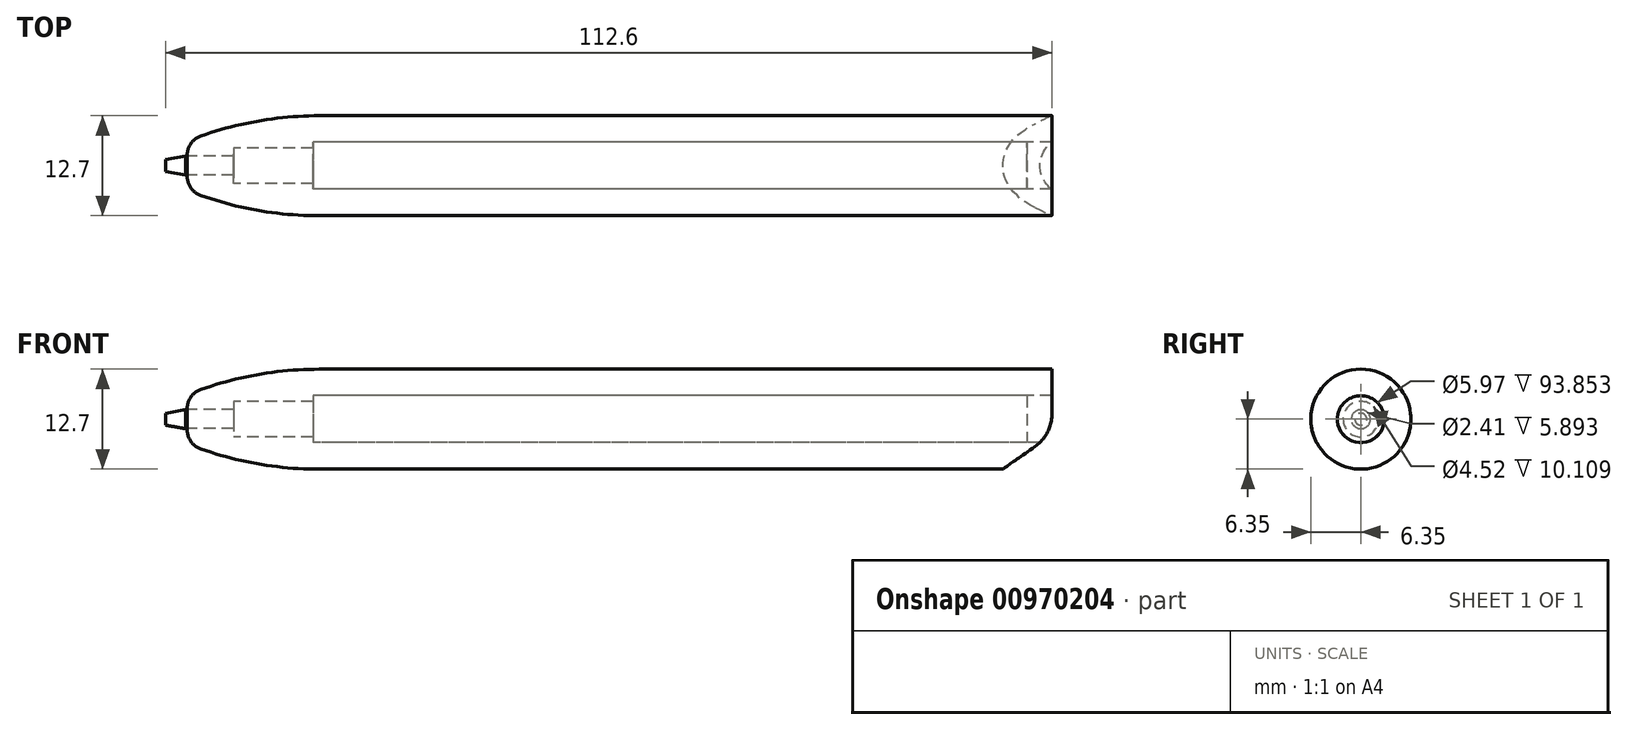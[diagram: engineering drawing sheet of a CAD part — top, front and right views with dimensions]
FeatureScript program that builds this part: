
annotation { "Feature Type Name" : "Feature", "Feature Type Description" : "" }
export const myFeature = defineFeature(function(context is Context, id is Id, definition is map)
    precondition{}
    {
        {
            var Q0;
            Q0=qCreatedBy(makeId("Front.planeOp"),FACE);
            var sketch = newSketch(context, id + "F0", { "sketchPlane" : qUnion([Q0])});
            skLineSegment(sketch, "E0", {"start": v(0, 0) * mm, "end": v(0, 2.98) * mm});
            skLineSegment(sketch, "E1", {"start": v(0, 2.98) * mm, "end": v(-90.68, 2.98) * mm});
            skLineSegment(sketch, "E2", {"start": v(-90.68, 2.98) * mm, "end": v(-90.68, 2.26) * mm});
            skLineSegment(sketch, "E3", {"start": v(-90.68, 2.26) * mm, "end": v(-100.79, 2.26) * mm});
            skLineSegment(sketch, "E4", {"start": v(-100.79, 1.55) * mm, "end": v(-100.79, 1.2) * mm});
            skLineSegment(sketch, "E5", {"start": v(-100.79, 1.2) * mm, "end": v(-109.42, 1.2) * mm});
            skLineSegment(sketch, "E6", {"start": v(-109.42, 1.2) * mm, "end": v(-109.42, 0) * mm});
            skLineSegment(sketch, "E7", {"start": v(-109.42, 0) * mm, "end": v(0, 0) * mm});
            skLineSegment(sketch, "E8", {"start": v(-100.79, 1.55) * mm, "end": v(-100.79, 2.26) * mm});
            skSolve(sketch);
        }
        {
            var Q0;
            Q0=makeQuery(id+"F0.imprint","IMPRINT",FACE,{"disambiguationData":[TD([[makeQuery(id+"F0.imprint","IMPRINT",EDGE,{"derivedFrom":sQuery(id+"F0.wireOp",EDGE,"E0")}),1.0]])]});
            var Q1;
            Q1=sQuery(id+"F0.wireOp",EDGE,"E7");
            revolve(context, id + "F1", {"surfaceOperationType" : NewSurfaceOperationType.NEW, "entities" : qUnion([Q0]), "axis" : qUnion([Q1]), "revolveType" : RevolveType.FULL});
        }
        {
            var Q0;
            Q0=qCreatedBy(makeId("Front.planeOp"),FACE);
            var sketch = newSketch(context, id + "F2", { "sketchPlane" : qUnion([Q0])});
            skLineSegment(sketch, "E9", {"start": v(-89.9, 6.35) * mm, "end": v(0, 6.35) * mm});
            skArc(sketch, "E10", {"start": v(-89.9, 6.35) * mm, "mid": v(-98.44, 5.54) * mm, "end": v(-106.68, 3.12) * mm});
            skLineSegment(sketch, "E11", {"start": v(-106.68, 3.12) * mm, "end": v(-106.68, 0) * mm});
            skLineSegment(sketch, "E12", {"start": v(-106.68, 0) * mm, "end": v(0, 0) * mm});
            skPoint(sketch, "E13.end.orphan", {"position": v(2.22, 6.35) * mm});
            skPoint(sketch, "E14.orphan", {"position": v(4.43, 6.35) * mm});
            skLineSegment(sketch, "E15", {"start": v(3.17, 0) * mm, "end": v(0, 0) * mm});
            skLineSegment(sketch, "E16", {"start": v(3.17, 0) * mm, "end": v(3.17, 6.35) * mm});
            skLineSegment(sketch, "E17", {"start": v(0, 6.35) * mm, "end": v(3.17, 6.35) * mm});
            skLineSegment(sketch, "E18.trimOffspring", {"start": v(4.36, 6.35) * mm, "end": v(4.43, 6.35) * mm});
            skSolve(sketch);
        }
        {
            var Q0;
            Q0=makeQuery(id+"F2.imprint","IMPRINT",FACE,{"disambiguationData":[TD([[makeQuery(id+"F2.imprint","IMPRINT",EDGE,{"derivedFrom":sQuery(id+"F2.wireOp",EDGE,"E9")}),-1.0]])]});
            var Q1;
            Q1=sQuery(id+"F2.wireOp",EDGE,"E9");
            var Q2;
            Q2=sQuery(id+"F2.wireOp",EDGE,"E10");
            var Q3;
            Q3=sQuery(id+"F2.wireOp",EDGE,"dEFs5qWQ-R8ky-eBhA-kIVd-nnHbt8vh1iMr");
            var Q4;
            Q4=sQuery(id+"F2.wireOp",EDGE,"E12");
            revolve(context, id + "F3", {"surfaceOperationType" : NewSurfaceOperationType.NEW, "entities" : qUnion([Q0]), "surfaceEntities" : qUnion([Q1, Q2, Q3]), "axis" : qUnion([Q4]), "revolveType" : RevolveType.FULL});
        }
        {
            var Q0;
            Q0=makeQuery(id+"F1.opRevolve","SWEPT_BODY",BODY,{"disambiguationData":[OSD([sQuery(id+"F0.wireOp",EDGE,"E0"),sQuery(id+"F0.wireOp",EDGE,"E1"),sQuery(id+"F0.wireOp",EDGE,"E2"),sQuery(id+"F0.wireOp",EDGE,"E3"),sQuery(id+"F0.wireOp",EDGE,"Mx4sm8FD-Cdkv-Anm1-aOvd-fS2C102Q7HrE"),sQuery(id+"F0.wireOp",EDGE,"LEFf2v4t-dNlz-Nh56-ndEK-DlUtqeBaB3i8"),sQuery(id+"F0.wireOp",EDGE,"E4"),sQuery(id+"F0.wireOp",EDGE,"E5"),sQuery(id+"F0.wireOp",EDGE,"E6"),sQuery(id+"F0.wireOp",EDGE,"E7")])]});
            var Q1;
            Q1=makeQuery(id+"F3.opRevolve","SWEPT_BODY",BODY,{"disambiguationData":[OSD([sQuery(id+"F2.wireOp",EDGE,"E9"),sQuery(id+"F2.wireOp",EDGE,"E10"),sQuery(id+"F2.wireOp",EDGE,"E11"),sQuery(id+"F2.wireOp",EDGE,"E12"),sQuery(id+"F2.wireOp",EDGE,"lBs16m9j-3z6w-QKKq-C0cc-swmu3a4mI5J7")])]});
            booleanBodies(context, id + "F4", {"operationType" : BooleanOperationType.SUBTRACTION, "tools" : qUnion([Q0]), "targets" : qUnion([Q1]), "keepTools" : true});
        }
        {
            var Q0;
            Q0=makeQuery(id+"F1.opRevolve","SWEPT_FACE",FACE,{"disambiguationData":[OSD([sQuery(id+"F0.wireOp",EDGE,"E0")])]});
            extrude(context, id + "F5", {"entities" : qUnion([Q0]), "operationType" : NewBodyOperationType.REMOVE, "depth" : 25.4 * mm, "offsetDistance" : 25.4 * mm});
        }
        {
            var Q0;
            Q0=qCreatedBy(makeId("Front.planeOp"),FACE);
            var sketch = newSketch(context, id + "F6", { "sketchPlane" : qUnion([Q0])});
            skLineSegment(sketch, "E19", {"start": v(-4.44, -7.3) * mm, "end": v(34.5, 19.97) * mm});
            skLineSegment(sketch, "E20", {"start": v(34.5, 19.97) * mm, "end": v(34.5, -25.4) * mm});
            skLineSegment(sketch, "E21", {"start": v(34.5, -25.4) * mm, "end": v(-4.44, -25.4) * mm});
            skLineSegment(sketch, "E22", {"start": v(-4.44, -25.4) * mm, "end": v(-4.44, -7.3) * mm});
            skSolve(sketch);
        }
        {
            var Q0;
            Q0=makeQuery(id+"F6.imprint","IMPRINT",FACE,{"disambiguationData":[TD([[makeQuery(id+"F6.imprint","IMPRINT",EDGE,{"derivedFrom":sQuery(id+"F6.wireOp",EDGE,"E19")}),-1.0]])]});
            extrude(context, id + "F7", {"entities" : qUnion([Q0]), "operationType" : NewBodyOperationType.REMOVE, "endBound" : BoundingType.SYMMETRIC, "oppositeDirection" : true, "depth" : 25.4 * mm, "offsetDistance" : 25.4 * mm});
        }
        {
            var Q0;
            Q0=makeQuery(id+"F7.boolean.opBoolean","INTERSECT",EDGE,{"disambiguationData":[OD(1.0)],"derivedFrom":[makeQuery(id+"F3.opRevolve","SWEPT_FACE",FACE,{"disambiguationData":[OSD([sQuery(id+"F2.wireOp",EDGE,"E16")])]}),makeQuery(id+"F7.opExtrude","SWEPT_FACE",FACE,{"disambiguationData":[OSD([sQuery(id+"F6.wireOp",EDGE,"E19")])]})]});
            var Q1;
            Q1=makeQuery(id+"F7.boolean.opBoolean","INTERSECT",EDGE,{"disambiguationData":[OD(0.0)],"derivedFrom":[makeQuery(id+"F3.opRevolve","SWEPT_FACE",FACE,{"disambiguationData":[OSD([sQuery(id+"F2.wireOp",EDGE,"E16")])]}),makeQuery(id+"F7.opExtrude","SWEPT_FACE",FACE,{"disambiguationData":[OSD([sQuery(id+"F6.wireOp",EDGE,"E19")])]})]});
            fillet(context, id + "F8", {"entities" : qUnion([Q0, Q1]), "tangentPropagation" : true, "radius" : 5.08 * mm, "defaultsChanged" : false, "vertexSettings" : [], "allowEdgeOverflow" : false});
        }
        {
            var Q0;
            Q0=makeQuery(id+"F1.opRevolve","SWEPT_EDGE",EDGE,{"disambiguationData":[OSD([sQuery(id+"F0.wireOp",EDGE,"E5"),sQuery(id+"F0.wireOp",EDGE,"E6")])]});
            chamfer(context, id + "F9", {"entities" : qUnion([Q0]), "chamferType" : ChamferType.OFFSET_ANGLE, "width" : 2.54 * mm, "oppositeDirection" : true, "angle" : 10 * degree, "tangentPropagation" : true});
        }
        {
            var Q0;
            Q0=makeQuery(id+"F3.opRevolve","SWEPT_EDGE",EDGE,{"disambiguationData":[OSD([sQuery(id+"F2.wireOp",EDGE,"E10"),sQuery(id+"F2.wireOp",EDGE,"E11")])]});
            fillet(context, id + "F10", {"entities" : qUnion([Q0]), "tangentPropagation" : true, "radius" : 2.54 * mm, "defaultsChanged" : false, "vertexSettings" : [], "allowEdgeOverflow" : false});
        }
    });
